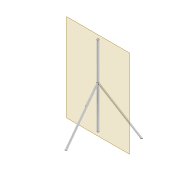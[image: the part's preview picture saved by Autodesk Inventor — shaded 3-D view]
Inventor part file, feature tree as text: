
AUTODESK INVENTOR PART (.ipt)
format: ipt  version: 2022 (Build 260153000, 153)  size: 95,744 bytes
history: native  units: mm
features: sketch x3, extrude x1, plane x1, loft x1, pattern_circular x1, projected_geometry x1
ambient origin geometry x8: Origin, YZ Plane, XZ Plane, XY Plane, X Axis, Y Axis, Z Axis, Center Point
bodies: Solid1 (feature_tree)
feature tree (8):
  extrude  "Extrusion1"  Depth=1500.0mm TaperAngle=0.0deg
  plane  "Work Plane1"
  loft  "Loft1"
  pattern_circular  "Circular Pattern1"  Count=60  [1 undecoded]
  sketch  "Sketch1"  dims[d0=34.5mm d1=1500.0mm d2=0.0mm]
  sketch  "Sketch2"  dims[d3=-800.0mm d4=34.5mm d5=600.0mm]
  projected_geometry  "Projected Loop1"
  sketch  "Sketch3"  dims[d6=0.0mm d7=90.0deg d8=0.0mm d9=90.0deg d10=30.0mm d11=360.0deg]
note: 1 required parameter value undecoded (feature->parameter linkage not recoverable at this tier; creation-order binding heuristic only, values carry confidence <= 0.55)
